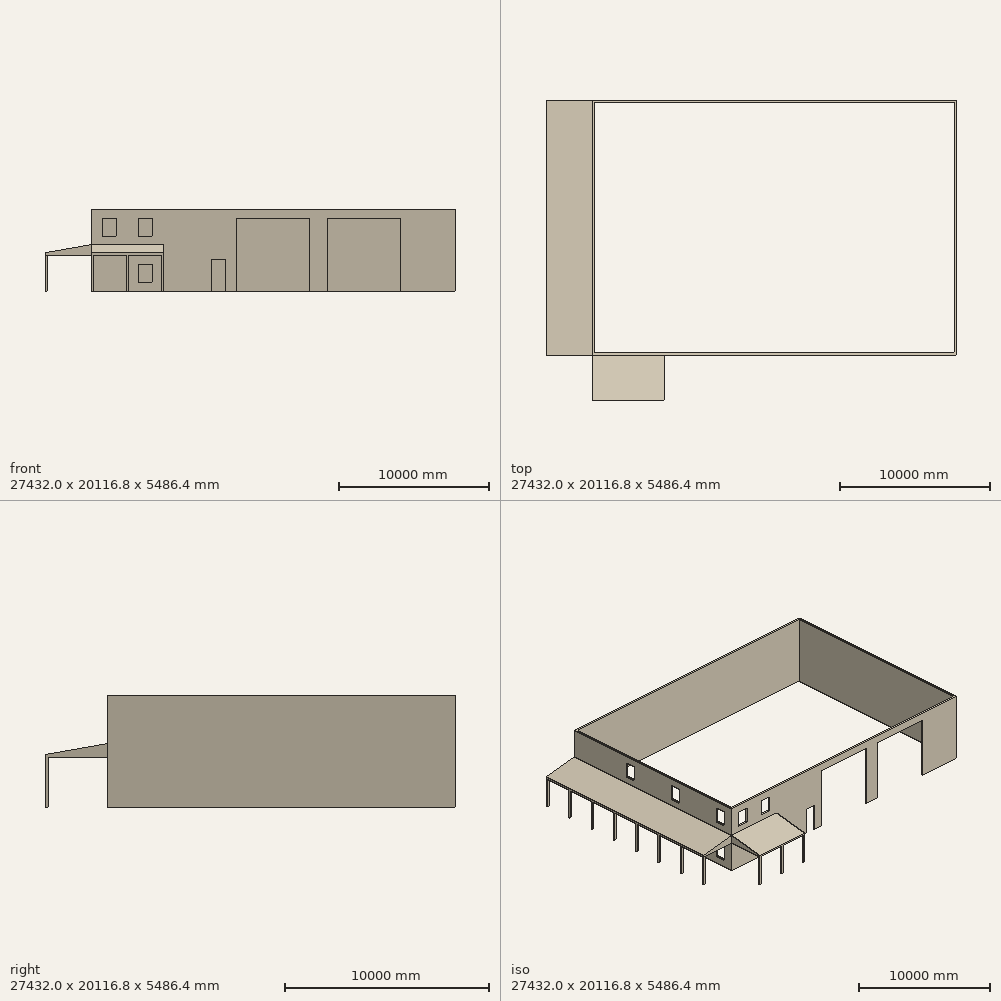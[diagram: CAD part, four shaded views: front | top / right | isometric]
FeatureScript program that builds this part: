
annotation { "Feature Type Name" : "Feature", "Feature Type Description" : "" }
export const myFeature = defineFeature(function(context is Context, id is Id, definition is map)
    precondition{}
    {
        {
            var Q0;
            Q0=qCreatedBy(makeId("Top.planeOp"),FACE);
            var sketch = newSketch(context, id + "F0", { "sketchPlane" : qUnion([Q0])});
            skLineSegment(sketch, "E0.bottom", {"start": v(-9120.48, 12115.99) * mm, "end": v(15263.52, 12115.99) * mm});
            skLineSegment(sketch, "E0.top", {"start": v(-9120.48, -4952.81) * mm, "end": v(15263.52, -4952.81) * mm});
            skLineSegment(sketch, "E0.left", {"start": v(-9120.48, 12115.99) * mm, "end": v(-9120.48, -4952.81) * mm});
            skLineSegment(sketch, "E0.right", {"start": v(15263.52, 12115.99) * mm, "end": v(15263.52, -4952.81) * mm});
            skLineSegment(sketch, "E1.bottom", {"start": v(-8968.08, 11963.59) * mm, "end": v(15111.12, 11963.59) * mm});
            skLineSegment(sketch, "E1.top", {"start": v(-8968.08, -4800.41) * mm, "end": v(15111.12, -4800.41) * mm});
            skLineSegment(sketch, "E1.left", {"start": v(-8968.08, 11963.59) * mm, "end": v(-8968.08, -4800.41) * mm});
            skLineSegment(sketch, "E1.right", {"start": v(15111.12, 11963.59) * mm, "end": v(15111.12, -4800.41) * mm});
            skSolve(sketch);
        }
        {
            var Q0;
            Q0 = qSketchRegion(id + "F0", true);
            extrude(context, id + "F1", {"entities" : qUnion([Q0]), "depth" : 5486.4 * mm, "offsetDistance" : 25.4 * mm});
        }
        {
            var Q0;
            Q0=makeQuery(id+"F1.opExtrude","SWEPT_FACE",FACE,{"disambiguationData":[OSD([sQuery(id+"F0.wireOp",EDGE,"E0.top")])]});
            var sketch = newSketch(context, id + "F2", { "sketchPlane" : qUnion([Q0])});
            skLineSegment(sketch, "E2.bottom", {"start": v(633.12, 0) * mm, "end": v(5509.92, 0) * mm});
            skLineSegment(sketch, "E2.top", {"start": v(633.12, 4876.8) * mm, "end": v(5509.92, 4876.8) * mm});
            skLineSegment(sketch, "E2.left", {"start": v(633.12, 0) * mm, "end": v(633.12, 4876.8) * mm});
            skLineSegment(sketch, "E2.right", {"start": v(5509.92, 0) * mm, "end": v(5509.92, 4876.8) * mm});
            skLineSegment(sketch, "E3.bottom", {"start": v(6729.12, 0) * mm, "end": v(11605.92, 0) * mm});
            skLineSegment(sketch, "E3.top", {"start": v(6729.12, 4876.8) * mm, "end": v(11605.92, 4876.8) * mm});
            skLineSegment(sketch, "E3.left", {"start": v(6729.12, 0) * mm, "end": v(6729.12, 4876.8) * mm});
            skLineSegment(sketch, "E3.right", {"start": v(11605.92, 0) * mm, "end": v(11605.92, 4876.8) * mm});
            skLineSegment(sketch, "E4.bottom", {"start": v(-1043.28, 0) * mm, "end": v(-128.88, 0) * mm});
            skLineSegment(sketch, "E4.top", {"start": v(-1043.28, 2133.6) * mm, "end": v(-128.88, 2133.6) * mm});
            skLineSegment(sketch, "E4.left", {"start": v(-1043.28, 0) * mm, "end": v(-1043.28, 2133.6) * mm});
            skLineSegment(sketch, "E4.right", {"start": v(-128.88, 0) * mm, "end": v(-128.88, 2133.6) * mm});
            skSolve(sketch);
        }
        {
            var Q0;
            Q0 = qSketchRegion(id + "F2", true);
            extrude(context, id + "F3", {"entities" : qUnion([Q0]), "operationType" : NewBodyOperationType.REMOVE, "oppositeDirection" : true, "depth" : 177.8 * mm, "offsetDistance" : 25.4 * mm});
        }
        {
            var Q0;
            Q0=makeQuery(id+"F1.opExtrude","SWEPT_FACE",FACE,{"disambiguationData":[OSD([sQuery(id+"F0.wireOp",EDGE,"E0.top")])]});
            var sketch = newSketch(context, id + "F4", { "sketchPlane" : qUnion([Q0])});
            skLineSegment(sketch, "E5", {"start": v(-9120.48, 3128.24) * mm, "end": v(-12168.48, 2590.8) * mm});
            skLineSegment(sketch, "E6", {"start": v(-12168.48, 2590.8) * mm, "end": v(-12168.48, 2438.4) * mm});
            skLineSegment(sketch, "E7", {"start": v(-12168.48, 2438.4) * mm, "end": v(-9120.48, 2438.4) * mm});
            skLineSegment(sketch, "E8", {"start": v(-9120.48, 3128.24) * mm, "end": v(-9120.48, 2438.4) * mm});
            skSolve(sketch);
        }
        {
            var Q0;
            Q0 = qSketchRegion(id + "F4", true);
            extrude(context, id + "F5", {"entities" : qUnion([Q0]), "operationType" : NewBodyOperationType.ADD, "oppositeDirection" : true, "depth" : 17068.8 * mm, "offsetDistance" : 25.4 * mm});
        }
        {
            var Q0;
            {var subQ1=sQuery(id+"F4.wireOp",EDGE,"E7");var subQ5=sQuery(id+"F0.wireOp",EDGE,"E0.left");Q0=makeQuery(id+"F5.boolean.opBoolean","SPLIT",FACE,{"disambiguationData":[TD([makeQuery(id+"F5.opExtrude","SWEPT_FACE",FACE,{"disambiguationData":[OSD([subQ1])]})])],"derivedFrom":makeQuery(id+"F1.opExtrude","SWEPT_FACE",FACE,{"disambiguationData":[OSD([subQ5])]})});}
            var sketch = newSketch(context, id + "F6", { "sketchPlane" : qUnion([Q0])});
            skLineSegment(sketch, "E9", {"start": v(4952.81, 2438.4) * mm, "end": v(8000.81, 2438.4) * mm});
            skLineSegment(sketch, "E10", {"start": v(8000.81, 2438.4) * mm, "end": v(8000.81, 2590.8) * mm});
            skLineSegment(sketch, "E11", {"start": v(8000.81, 2590.8) * mm, "end": v(4952.81, 3128.24) * mm});
            skLineSegment(sketch, "E12", {"start": v(4952.81, 3128.24) * mm, "end": v(4952.81, 2438.4) * mm});
            skSolve(sketch);
        }
        {
            var Q0;
            Q0 = qSketchRegion(id + "F6", true);
            extrude(context, id + "F7", {"entities" : qUnion([Q0]), "operationType" : NewBodyOperationType.ADD, "oppositeDirection" : true, "depth" : 4876.8 * mm, "offsetDistance" : 25.4 * mm});
        }
        {
            var Q0;
            Q0=makeQuery(id+"F5.opExtrude","SWEPT_FACE",FACE,{"disambiguationData":[OSD([sQuery(id+"F4.wireOp",EDGE,"E7")])]});
            var sketch = newSketch(context, id + "F8", { "sketchPlane" : qUnion([Q0])});
            skLineSegment(sketch, "E13.bottom", {"start": v(-12168.48, -12115.99) * mm, "end": v(-12016.08, -12115.99) * mm});
            skLineSegment(sketch, "E13.top", {"start": v(-12168.48, -11963.59) * mm, "end": v(-12016.08, -11963.59) * mm});
            skLineSegment(sketch, "E13.left", {"start": v(-12168.48, -12115.99) * mm, "end": v(-12168.48, -11963.59) * mm});
            skLineSegment(sketch, "E13.right", {"start": v(-12016.08, -12115.99) * mm, "end": v(-12016.08, -11963.59) * mm});
            skLineSegment(sketch, "E14.0.1.0", {"start": v(-12168.48, -9544.24) * mm, "end": v(-12016.08, -9544.24) * mm});
            skLineSegment(sketch, "E14.0.1.1", {"start": v(-12168.48, -9696.64) * mm, "end": v(-12168.48, -9544.24) * mm});
            skLineSegment(sketch, "E14.0.1.2", {"start": v(-12016.08, -9696.64) * mm, "end": v(-12016.08, -9544.24) * mm});
            skLineSegment(sketch, "E14.0.1.3", {"start": v(-12168.48, -9696.64) * mm, "end": v(-12016.08, -9696.64) * mm});
            skLineSegment(sketch, "E14.0.2.0", {"start": v(-12168.48, -7124.89) * mm, "end": v(-12016.08, -7124.89) * mm});
            skLineSegment(sketch, "E14.0.2.1", {"start": v(-12168.48, -7277.29) * mm, "end": v(-12168.48, -7124.89) * mm});
            skLineSegment(sketch, "E14.0.2.2", {"start": v(-12016.08, -7277.29) * mm, "end": v(-12016.08, -7124.89) * mm});
            skLineSegment(sketch, "E14.0.2.3", {"start": v(-12168.48, -7277.29) * mm, "end": v(-12016.08, -7277.29) * mm});
            skLineSegment(sketch, "E14.0.3.0", {"start": v(-12168.48, -4705.54) * mm, "end": v(-12016.08, -4705.54) * mm});
            skLineSegment(sketch, "E14.0.3.1", {"start": v(-12168.48, -4857.94) * mm, "end": v(-12168.48, -4705.54) * mm});
            skLineSegment(sketch, "E14.0.3.2", {"start": v(-12016.08, -4857.94) * mm, "end": v(-12016.08, -4705.54) * mm});
            skLineSegment(sketch, "E14.0.3.3", {"start": v(-12168.48, -4857.94) * mm, "end": v(-12016.08, -4857.94) * mm});
            skLineSegment(sketch, "E14.0.4.0", {"start": v(-12168.48, -2286.19) * mm, "end": v(-12016.08, -2286.19) * mm});
            skLineSegment(sketch, "E14.0.4.1", {"start": v(-12168.48, -2438.59) * mm, "end": v(-12168.48, -2286.19) * mm});
            skLineSegment(sketch, "E14.0.4.2", {"start": v(-12016.08, -2438.59) * mm, "end": v(-12016.08, -2286.19) * mm});
            skLineSegment(sketch, "E14.0.4.3", {"start": v(-12168.48, -2438.59) * mm, "end": v(-12016.08, -2438.59) * mm});
            skLineSegment(sketch, "E14.0.5.0", {"start": v(-12168.48, 133.16) * mm, "end": v(-12016.08, 133.16) * mm});
            skLineSegment(sketch, "E14.0.5.1", {"start": v(-12168.48, -19.24) * mm, "end": v(-12168.48, 133.16) * mm});
            skLineSegment(sketch, "E14.0.5.2", {"start": v(-12016.08, -19.24) * mm, "end": v(-12016.08, 133.16) * mm});
            skLineSegment(sketch, "E14.0.5.3", {"start": v(-12168.48, -19.24) * mm, "end": v(-12016.08, -19.24) * mm});
            skLineSegment(sketch, "E14.0.6.0", {"start": v(-12168.48, 2552.51) * mm, "end": v(-12016.08, 2552.51) * mm});
            skLineSegment(sketch, "E14.0.6.1", {"start": v(-12168.48, 2400.11) * mm, "end": v(-12168.48, 2552.51) * mm});
            skLineSegment(sketch, "E14.0.6.2", {"start": v(-12016.08, 2400.11) * mm, "end": v(-12016.08, 2552.51) * mm});
            skLineSegment(sketch, "E14.0.6.3", {"start": v(-12168.48, 2400.11) * mm, "end": v(-12016.08, 2400.11) * mm});
            skLineSegment(sketch, "E14.0.7.0", {"start": v(-12168.48, 4971.86) * mm, "end": v(-12016.08, 4971.86) * mm});
            skLineSegment(sketch, "E14.0.7.1", {"start": v(-12168.48, 4819.46) * mm, "end": v(-12168.48, 4971.86) * mm});
            skLineSegment(sketch, "E14.0.7.2", {"start": v(-12016.08, 4819.46) * mm, "end": v(-12016.08, 4971.86) * mm});
            skLineSegment(sketch, "E14.0.7.3", {"start": v(-12168.48, 4819.46) * mm, "end": v(-12016.08, 4819.46) * mm});
            skLineSegment(sketch, "E14.direction1", {"start": v(-12168.48, -12115.99) * mm, "end": v(-12168.48, -12115.99) * mm});
            skLineSegment(sketch, "E14.direction2", {"start": v(-12168.48, -12115.99) * mm, "end": v(-12168.48, -9696.64) * mm, "construction": true});
            skSolve(sketch);
        }
        {
            var Q0;
            Q0 = qSketchRegion(id + "F8", true);
            extrude(context, id + "F9", {"entities" : qUnion([Q0]), "operationType" : NewBodyOperationType.ADD, "depth" : 2438.4 * mm, "offsetDistance" : 25.4 * mm});
        }
        {
            var Q0;
            Q0=makeQuery(id+"F7.opExtrude","SWEPT_FACE",FACE,{"disambiguationData":[OSD([sQuery(id+"F6.wireOp",EDGE,"E9")])]});
            var sketch = newSketch(context, id + "F10", { "sketchPlane" : qUnion([Q0])});
            skLineSegment(sketch, "E15.bottom", {"start": v(-4243.68, 8000.81) * mm, "end": v(-4396.08, 8000.81) * mm});
            skLineSegment(sketch, "E15.top", {"start": v(-4243.68, 7848.41) * mm, "end": v(-4396.08, 7848.41) * mm});
            skLineSegment(sketch, "E15.left", {"start": v(-4243.68, 8000.81) * mm, "end": v(-4243.68, 7848.41) * mm});
            skLineSegment(sketch, "E15.right", {"start": v(-4396.08, 8000.81) * mm, "end": v(-4396.08, 7848.41) * mm});
            skLineSegment(sketch, "E16.1.0.0", {"start": v(-6605.88, 8000.81) * mm, "end": v(-6758.28, 8000.81) * mm});
            skLineSegment(sketch, "E16.1.0.1", {"start": v(-6605.88, 7848.41) * mm, "end": v(-6758.28, 7848.41) * mm});
            skLineSegment(sketch, "E16.1.0.2", {"start": v(-6758.28, 8000.81) * mm, "end": v(-6758.28, 7848.41) * mm});
            skLineSegment(sketch, "E16.1.0.3", {"start": v(-6605.88, 8000.81) * mm, "end": v(-6605.88, 7848.41) * mm});
            skLineSegment(sketch, "E16.2.0.0", {"start": v(-8968.08, 8000.81) * mm, "end": v(-9120.48, 8000.81) * mm});
            skLineSegment(sketch, "E16.2.0.1", {"start": v(-8968.08, 7848.41) * mm, "end": v(-9120.48, 7848.41) * mm});
            skLineSegment(sketch, "E16.2.0.2", {"start": v(-9120.48, 8000.81) * mm, "end": v(-9120.48, 7848.41) * mm});
            skLineSegment(sketch, "E16.2.0.3", {"start": v(-8968.08, 8000.81) * mm, "end": v(-8968.08, 7848.41) * mm});
            skLineSegment(sketch, "E16.direction1", {"start": v(-4396.08, 7848.41) * mm, "end": v(-6758.28, 7848.41) * mm, "construction": true});
            skSolve(sketch);
        }
        {
            var Q0;
            Q0 = qSketchRegion(id + "F10", true);
            extrude(context, id + "F11", {"entities" : qUnion([Q0]), "operationType" : NewBodyOperationType.ADD, "depth" : 2438.4 * mm, "offsetDistance" : 25.4 * mm});
        }
        {
            var Q0;
            {var subQ1=sQuery(id+"F4.wireOp",EDGE,"E7");var subQ5=sQuery(id+"F0.wireOp",EDGE,"E0.left");Q0=makeQuery(id+"F5.boolean.opBoolean","SPLIT",FACE,{"disambiguationData":[TD([makeQuery(id+"F5.opExtrude","SWEPT_FACE",FACE,{"disambiguationData":[OSD([subQ1])]})])],"derivedFrom":makeQuery(id+"F1.opExtrude","SWEPT_FACE",FACE,{"disambiguationData":[OSD([subQ5])]})});}
            var sketch = newSketch(context, id + "F12", { "sketchPlane" : qUnion([Q0])});
            skLineSegment(sketch, "E17.bottom", {"start": v(-4038.79, 0) * mm, "end": v(-3124.39, 0) * mm});
            skLineSegment(sketch, "E17.top", {"start": v(-4038.79, 2032) * mm, "end": v(-3124.39, 2032) * mm});
            skLineSegment(sketch, "E17.left", {"start": v(-4038.79, 0) * mm, "end": v(-4038.79, 2032) * mm});
            skLineSegment(sketch, "E17.right", {"start": v(-3124.39, 0) * mm, "end": v(-3124.39, 2032) * mm});
            skLineSegment(sketch, "E18.bottom", {"start": v(-11353.99, 1828.8) * mm, "end": v(-10439.59, 1828.8) * mm});
            skLineSegment(sketch, "E18.top", {"start": v(-11353.99, 609.6) * mm, "end": v(-10439.59, 609.6) * mm});
            skLineSegment(sketch, "E18.left", {"start": v(-11353.99, 1828.8) * mm, "end": v(-11353.99, 609.6) * mm});
            skLineSegment(sketch, "E18.right", {"start": v(-10439.59, 1828.8) * mm, "end": v(-10439.59, 609.6) * mm});
            skLineSegment(sketch, "E19.bottom", {"start": v(-6477.19, 1828.8) * mm, "end": v(-5562.79, 1828.8) * mm});
            skLineSegment(sketch, "E19.top", {"start": v(-6477.19, 609.6) * mm, "end": v(-5562.79, 609.6) * mm});
            skLineSegment(sketch, "E19.left", {"start": v(-6477.19, 1828.8) * mm, "end": v(-6477.19, 609.6) * mm});
            skLineSegment(sketch, "E19.right", {"start": v(-5562.79, 1828.8) * mm, "end": v(-5562.79, 609.6) * mm});
            skLineSegment(sketch, "E20.bottom", {"start": v(-1600.39, 1828.8) * mm, "end": v(-685.99, 1828.8) * mm});
            skLineSegment(sketch, "E20.top", {"start": v(-1600.39, 609.6) * mm, "end": v(-685.99, 609.6) * mm});
            skLineSegment(sketch, "E20.left", {"start": v(-1600.39, 1828.8) * mm, "end": v(-1600.39, 609.6) * mm});
            skLineSegment(sketch, "E20.right", {"start": v(-685.99, 1828.8) * mm, "end": v(-685.99, 609.6) * mm});
            skLineSegment(sketch, "E21.bottom", {"start": v(3276.41, 1828.8) * mm, "end": v(4190.81, 1828.8) * mm});
            skLineSegment(sketch, "E21.top", {"start": v(3276.41, 609.6) * mm, "end": v(4190.81, 609.6) * mm});
            skLineSegment(sketch, "E21.left", {"start": v(3276.41, 1828.8) * mm, "end": v(3276.41, 609.6) * mm});
            skLineSegment(sketch, "E21.right", {"start": v(4190.81, 1828.8) * mm, "end": v(4190.81, 609.6) * mm});
            skSolve(sketch);
        }
        {
            var Q0;
            Q0 = qSketchRegion(id + "F12", true);
            extrude(context, id + "F13", {"entities" : qUnion([Q0]), "operationType" : NewBodyOperationType.REMOVE, "oppositeDirection" : true, "depth" : 152.4 * mm, "offsetDistance" : 25.4 * mm});
        }
        {
            var Q0;
            {var subQ0=sQuery(id+"F4.wireOp",EDGE,"E5");var subQ1=sQuery(id+"F0.wireOp",EDGE,"E0.right");var subQ7=sQuery(id+"F0.wireOp",EDGE,"E0.top");var subQ9=makeQuery(id+"F1.opExtrude","SWEPT_FACE",FACE,{"disambiguationData":[OSD([subQ7])]});var subQ10=sQuery(id+"F4.wireOp",EDGE,"E7");var subQ11=makeQuery(id+"F5.opExtrude","CAP_FACE",FACE,{"disambiguationData":[OSD([subQ0,sQuery(id+"F4.wireOp",EDGE,"E6"),subQ10,sQuery(id+"F4.wireOp",EDGE,"E8")])],"isStart":true});Q0=makeQuery(id+"F7.boolean.opBoolean","SPLIT",FACE,{"disambiguationData":[TD([makeQuery(id+"F1.opExtrude","SWEPT_FACE",FACE,{"disambiguationData":[OSD([subQ1])]})])],"derivedFrom":makeQuery(id+"F5.boolean.opBoolean","MERGE",FACE,{"derivedFrom":[subQ9,subQ11]})});}
            var sketch = newSketch(context, id + "F14", { "sketchPlane" : qUnion([Q0])});
            skLineSegment(sketch, "E22.bottom", {"start": v(-5920.08, 1828.8) * mm, "end": v(-5005.68, 1828.8) * mm});
            skLineSegment(sketch, "E22.top", {"start": v(-5920.08, 609.6) * mm, "end": v(-5005.68, 609.6) * mm});
            skLineSegment(sketch, "E22.left", {"start": v(-5920.08, 1828.8) * mm, "end": v(-5920.08, 609.6) * mm});
            skLineSegment(sketch, "E22.right", {"start": v(-5005.68, 1828.8) * mm, "end": v(-5005.68, 609.6) * mm});
            skSolve(sketch);
        }
        {
            var Q0;
            Q0 = qSketchRegion(id + "F14", true);
            extrude(context, id + "F15", {"entities" : qUnion([Q0]), "operationType" : NewBodyOperationType.REMOVE, "oppositeDirection" : true, "depth" : 152.4 * mm, "offsetDistance" : 25.4 * mm});
        }
        {
            var Q0;
            {var subQ1=sQuery(id+"F4.wireOp",EDGE,"E5");var subQ2=sQuery(id+"F0.wireOp",EDGE,"E0.left");Q0=makeQuery(id+"F5.boolean.opBoolean","SPLIT",FACE,{"disambiguationData":[TD([makeQuery(id+"F5.opExtrude","SWEPT_FACE",FACE,{"disambiguationData":[OSD([subQ1])]})])],"derivedFrom":makeQuery(id+"F1.opExtrude","SWEPT_FACE",FACE,{"disambiguationData":[OSD([subQ2])]})});}
            var sketch = newSketch(context, id + "F16", { "sketchPlane" : qUnion([Q0])});
            skLineSegment(sketch, "E23.bottom", {"start": v(-1600.39, 4876.8) * mm, "end": v(-685.99, 4876.8) * mm});
            skLineSegment(sketch, "E23.top", {"start": v(-1600.39, 3657.6) * mm, "end": v(-685.99, 3657.6) * mm});
            skLineSegment(sketch, "E23.left", {"start": v(-1600.39, 4876.8) * mm, "end": v(-1600.39, 3657.6) * mm});
            skLineSegment(sketch, "E23.right", {"start": v(-685.99, 4876.8) * mm, "end": v(-685.99, 3657.6) * mm});
            skLineSegment(sketch, "E24.bottom", {"start": v(3276.41, 4876.8) * mm, "end": v(4190.81, 4876.8) * mm});
            skLineSegment(sketch, "E24.top", {"start": v(3276.41, 3657.6) * mm, "end": v(4190.81, 3657.6) * mm});
            skLineSegment(sketch, "E24.left", {"start": v(3276.41, 4876.8) * mm, "end": v(3276.41, 3657.6) * mm});
            skLineSegment(sketch, "E24.right", {"start": v(4190.81, 4876.8) * mm, "end": v(4190.81, 3657.6) * mm});
            skLineSegment(sketch, "E25.bottom", {"start": v(-6477.19, 4876.8) * mm, "end": v(-5562.79, 4876.8) * mm});
            skLineSegment(sketch, "E25.top", {"start": v(-6477.19, 3657.6) * mm, "end": v(-5562.79, 3657.6) * mm});
            skLineSegment(sketch, "E25.left", {"start": v(-6477.19, 4876.8) * mm, "end": v(-6477.19, 3657.6) * mm});
            skLineSegment(sketch, "E25.right", {"start": v(-5562.79, 4876.8) * mm, "end": v(-5562.79, 3657.6) * mm});
            skSolve(sketch);
        }
        {
            var Q0;
            Q0 = qSketchRegion(id + "F16", true);
            extrude(context, id + "F17", {"entities" : qUnion([Q0]), "operationType" : NewBodyOperationType.REMOVE, "endBound" : BoundingType.UP_TO_NEXT, "oppositeDirection" : true, "depth" : 25.4 * mm, "offsetDistance" : 25.4 * mm});
        }
        {
            var Q0;
            {var subQ0=sQuery(id+"F4.wireOp",EDGE,"E5");var subQ1=sQuery(id+"F0.wireOp",EDGE,"E0.right");var subQ7=sQuery(id+"F0.wireOp",EDGE,"E0.top");var subQ9=makeQuery(id+"F1.opExtrude","SWEPT_FACE",FACE,{"disambiguationData":[OSD([subQ7])]});var subQ10=sQuery(id+"F4.wireOp",EDGE,"E7");var subQ11=makeQuery(id+"F5.opExtrude","CAP_FACE",FACE,{"disambiguationData":[OSD([subQ0,sQuery(id+"F4.wireOp",EDGE,"E6"),subQ10,sQuery(id+"F4.wireOp",EDGE,"E8")])],"isStart":true});Q0=makeQuery(id+"F7.boolean.opBoolean","SPLIT",FACE,{"disambiguationData":[TD([makeQuery(id+"F1.opExtrude","SWEPT_FACE",FACE,{"disambiguationData":[OSD([subQ1])]})])],"derivedFrom":makeQuery(id+"F5.boolean.opBoolean","MERGE",FACE,{"derivedFrom":[subQ9,subQ11]})});}
            var sketch = newSketch(context, id + "F18", { "sketchPlane" : qUnion([Q0])});
            skLineSegment(sketch, "E26.bottom", {"start": v(-8358.48, 4876.8) * mm, "end": v(-7444.08, 4876.8) * mm});
            skLineSegment(sketch, "E26.top", {"start": v(-8358.48, 3657.6) * mm, "end": v(-7444.08, 3657.6) * mm});
            skLineSegment(sketch, "E26.left", {"start": v(-8358.48, 4876.8) * mm, "end": v(-8358.48, 3657.6) * mm});
            skLineSegment(sketch, "E26.right", {"start": v(-7444.08, 4876.8) * mm, "end": v(-7444.08, 3657.6) * mm});
            skLineSegment(sketch, "E27.bottom", {"start": v(-5920.08, 4876.8) * mm, "end": v(-5005.68, 4876.8) * mm});
            skLineSegment(sketch, "E27.top", {"start": v(-5920.08, 3657.6) * mm, "end": v(-5005.68, 3657.6) * mm});
            skLineSegment(sketch, "E27.left", {"start": v(-5920.08, 4876.8) * mm, "end": v(-5920.08, 3657.6) * mm});
            skLineSegment(sketch, "E27.right", {"start": v(-5005.68, 4876.8) * mm, "end": v(-5005.68, 3657.6) * mm});
            skSolve(sketch);
        }
        {
            var Q0;
            Q0 = qSketchRegion(id + "F18", true);
            extrude(context, id + "F19", {"entities" : qUnion([Q0]), "operationType" : NewBodyOperationType.REMOVE, "endBound" : BoundingType.UP_TO_NEXT, "oppositeDirection" : true, "depth" : 25.4 * mm, "offsetDistance" : 25.4 * mm});
        }
    });
